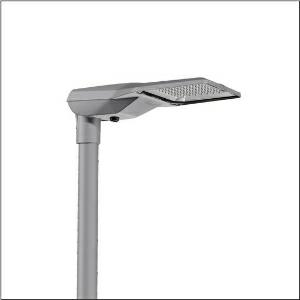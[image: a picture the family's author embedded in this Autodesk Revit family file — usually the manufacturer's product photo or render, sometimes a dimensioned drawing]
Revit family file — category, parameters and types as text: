
# Revit family: streetlight_sl_21_midi___st1_0a_5xe3d33r08nb_ea4c
name_source: partatom
category: Lighting Fixtures
units: mm (PartAtom-declared; Revit-internal decimal feet)

## family parameters
Cut with Voids When Loaded = No
Host = Face
Light Source = No
Part Type = Normal
Room Calculation Point = No
Round Connector Dimension = Use Diameter
Shared = No

## types (1)
- --- (1 x LED, 22700 lm, 151.2 W, 3000K)
    Apparent Load = 151 VA
    CIE Flux Codes = 40 73 97 100 100
    Color Rendering = 70
    Color Temperature = 3000K
    Default Elevation = 1800 mm
    Description = Streetlight SL 21 midi, mast luminaire, primary light control with lens, of PMMA, primary optical cover: cover, of toughened safety glass, transparent, light distribution: ST1.0a, light emission: direct distribution, primary light characteristic: asymmetric, installation type: side-entry, post-top, LED, High Power LED, rated luminous flux: 22.700lm, luminous efficacy: 150lm/W, light colour: 730, colour temperature: 3000K, control gear: D4i, control: flexible luminous flux parameterisation, time-dependent luminous flux control, constant luminous flux control, overheat protection, pre-setting: logarithmic dimming characteristic, mains connection: 230..240V, AC, 50/60Hz, start of lifetime: 151W, end of service life: 157W, reduction: 70W, luminaire housing, of diecast aluminium, powder-coated, SITECO metallic grey (DB 702S), corrosivity category C5 high according to DIN EN ISO 12944, please order mast flange separately, inclination adjustable: 0°, 5°, 10°, 15°, sealing non-destructively replaceable, multi-level sealing system, length: 644mm, width: 335mm, height: 110mm, mast flange for spigot size: 42mm (side-entry): 5XC10008XM4, 60/48mm (side-entry/post-top): 5XC10108XM2, 76/60mm (side-entry/post-top): 5XC10108XM1, mounting height: 4..8m, Smart Interface below, protection rating (complete): IP66, insulation class (complete): insulation class II (safety insulation), certification: CE, ENEC, ENEC+, VDE, impact resistance: IK10, permissible operating ambient temperature for outdoor applications: -40..+50°C, standard-compliant lighting for roads and squares, packaging unit: 1 piece

Light Distribution: ST1.0a
    Height = 111 mm
    Lamp = 1 x LED
    Lamp Light Flux = 22700 lm
    Lamp Power = 151.2 W
    Lamp count = 1
    Length = 644 mm
    Luminous efficacy = 150 lm/W
    Manufacturer = Siteco
    ModVariant = No
    Model = 5XE3D33R08NB
    Number of Poles = 1
    OnlyDefault = Yes
    Power Factor = 1
    Product Name = Streetlight SL 21 midi | ST1.0a
    Product group = mast luminaire | pylon top
    ProductGroupID = 6100
    Protection Class = Protection class II
    Protection Degree = IP 66
    RLX_Detail_Level = 1
    RLX_Emergency_Light_Flux = 0 lm
    RLX_Emergency_Type = 0
    RLX_Emergency_Type_DB = No
    RlxData = <blob elided: 27093 chars, md5=0e44328b>
    Socket = socket
    Standby Power = 0 W
    System Light Flux = 22700 lm
    System Power = 151 W
    Type Comments = factory setting: luminous flux: 100 % | dim-lin: 254 | 802 mA
    Type Image = l_1004300.jpg
    URL = http://relux.com
    VarID = @adj_170129
    Voltage = 0 V
    Weight = 0.00 kg
    Width = 336 mm

## geometry (parser evidence)
native form markers: Blend x4, Sweep x10
no freeform markers — native parametric forms only
